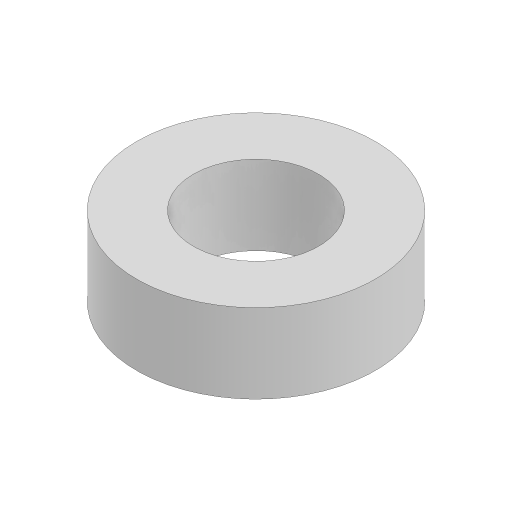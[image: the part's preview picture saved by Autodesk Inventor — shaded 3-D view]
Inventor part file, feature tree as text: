
AUTODESK INVENTOR PART (.ipt)
format: ipt  version: 2024 (Build 280153000, 153)  size: 98,816 bytes
history: native  units: mm
features: extrude x1, direct_edit x1, sketch x1, other x1
ambient origin geometry x8: Origin, YZ Plane, XZ Plane, XY Plane, X Axis, Y Axis, Z Axis, Center Point
bodies: Solid1 (feature_tree)
feature tree (4):
  extrude  "Extrusion1"  Depth=6.35mm
  direct_edit  "Direct Edit1"
  sketch  "Sketch1"  dims[d0=9.525mm d1=4.8mm d2=6.35mm d3=0.0mm d4=-0.254mm]
  other  "Size1"
